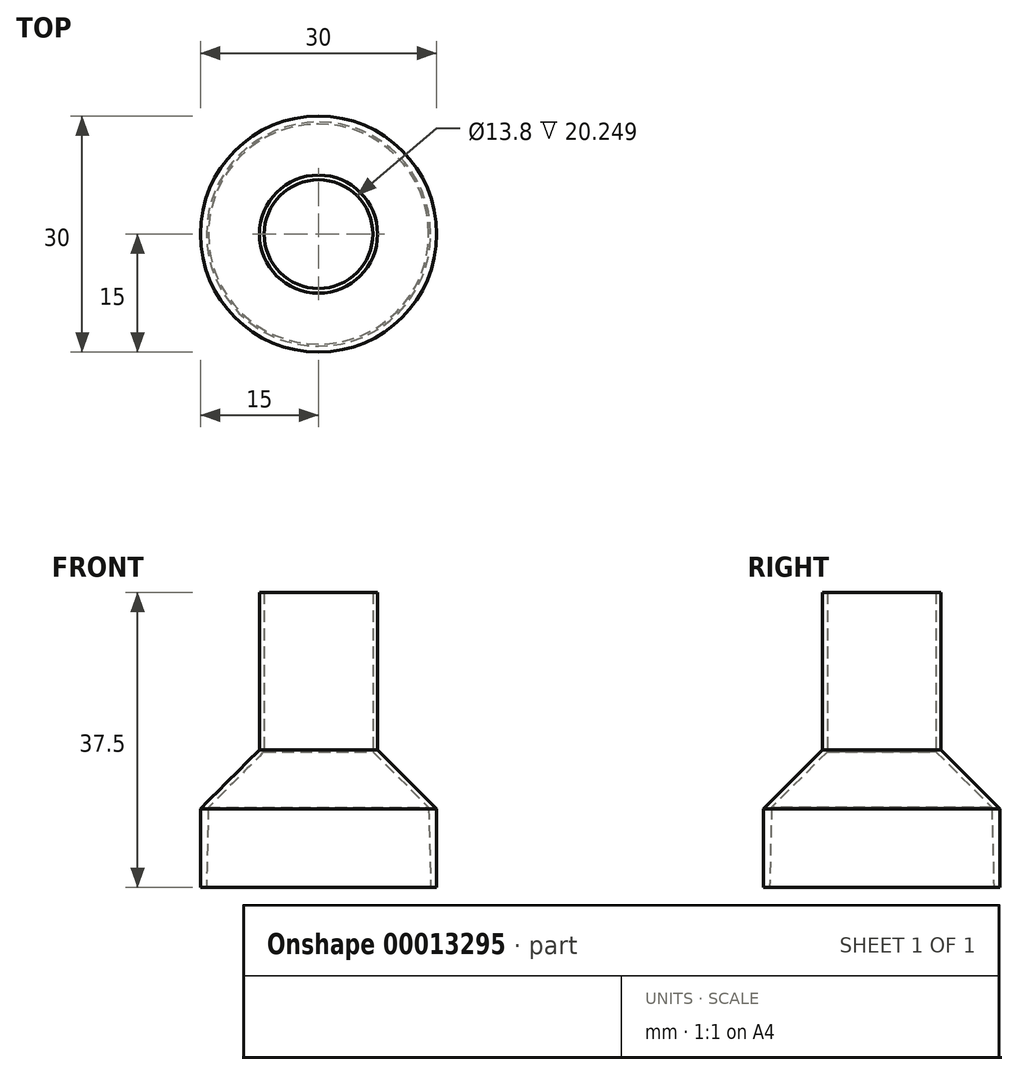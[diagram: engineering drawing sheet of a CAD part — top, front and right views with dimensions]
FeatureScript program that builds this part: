
annotation { "Feature Type Name" : "Feature", "Feature Type Description" : "" }
export const myFeature = defineFeature(function(context is Context, id is Id, definition is map)
    precondition{}
    {
        {
            var Q0;
            Q0=qCreatedBy(makeId("Front.planeOp"),FACE);
            var sketch = newSketch(context, id + "F0", { "sketchPlane" : qUnion([Q0])});
            skLineSegment(sketch, "E0", {"start": v(-15, 0) * mm, "end": v(-15, 10) * mm});
            skLineSegment(sketch, "E1", {"start": v(-15, 10) * mm, "end": v(-7.5, 17.5) * mm});
            skLineSegment(sketch, "E2", {"start": v(-7.5, 17.5) * mm, "end": v(-7.5, 37.5) * mm});
            skLineSegment(sketch, "E3.0", {"start": v(-6.9, 17.25) * mm, "end": v(-6.9, 37.5) * mm});
            skLineSegment(sketch, "E3.1", {"start": v(-13.99, 10.16) * mm, "end": v(-6.9, 17.25) * mm});
            skLineSegment(sketch, "E3.2", {"start": v(-14.24, 0) * mm, "end": v(-13.99, 10.16) * mm});
            skLineSegment(sketch, "E4", {"start": v(-7.5, 37.5) * mm, "end": v(-6.9, 37.5) * mm});
            skLineSegment(sketch, "E5", {"start": v(-14.24, 0) * mm, "end": v(-15, 0) * mm});
            skLineSegment(sketch, "E6", {"start": v(0, 0) * mm, "end": v(0, 37.5) * mm, "construction": true});
            skLineSegment(sketch, "E7", {"start": v(-13.99, 10.16) * mm, "end": v(-13.99, 0) * mm, "construction": true});
            skSolve(sketch);
        }
        {
            var Q0;
            Q0=makeQuery(id+"F0.imprint","IMPRINT",FACE,{"disambiguationData":[TD([[makeQuery(id+"F0.imprint","IMPRINT",EDGE,{"derivedFrom":sQuery(id+"F0.wireOp",EDGE,"E0")}),-1.0]])]});
            var Q1;
            Q1=sQuery(id+"F0.wireOp",EDGE,"E6");
            revolve(context, id + "F1", {"surfaceOperationType" : NewSurfaceOperationType.NEW, "entities" : qUnion([Q0]), "axis" : qUnion([Q1]), "revolveType" : RevolveType.FULL});
        }
    });
